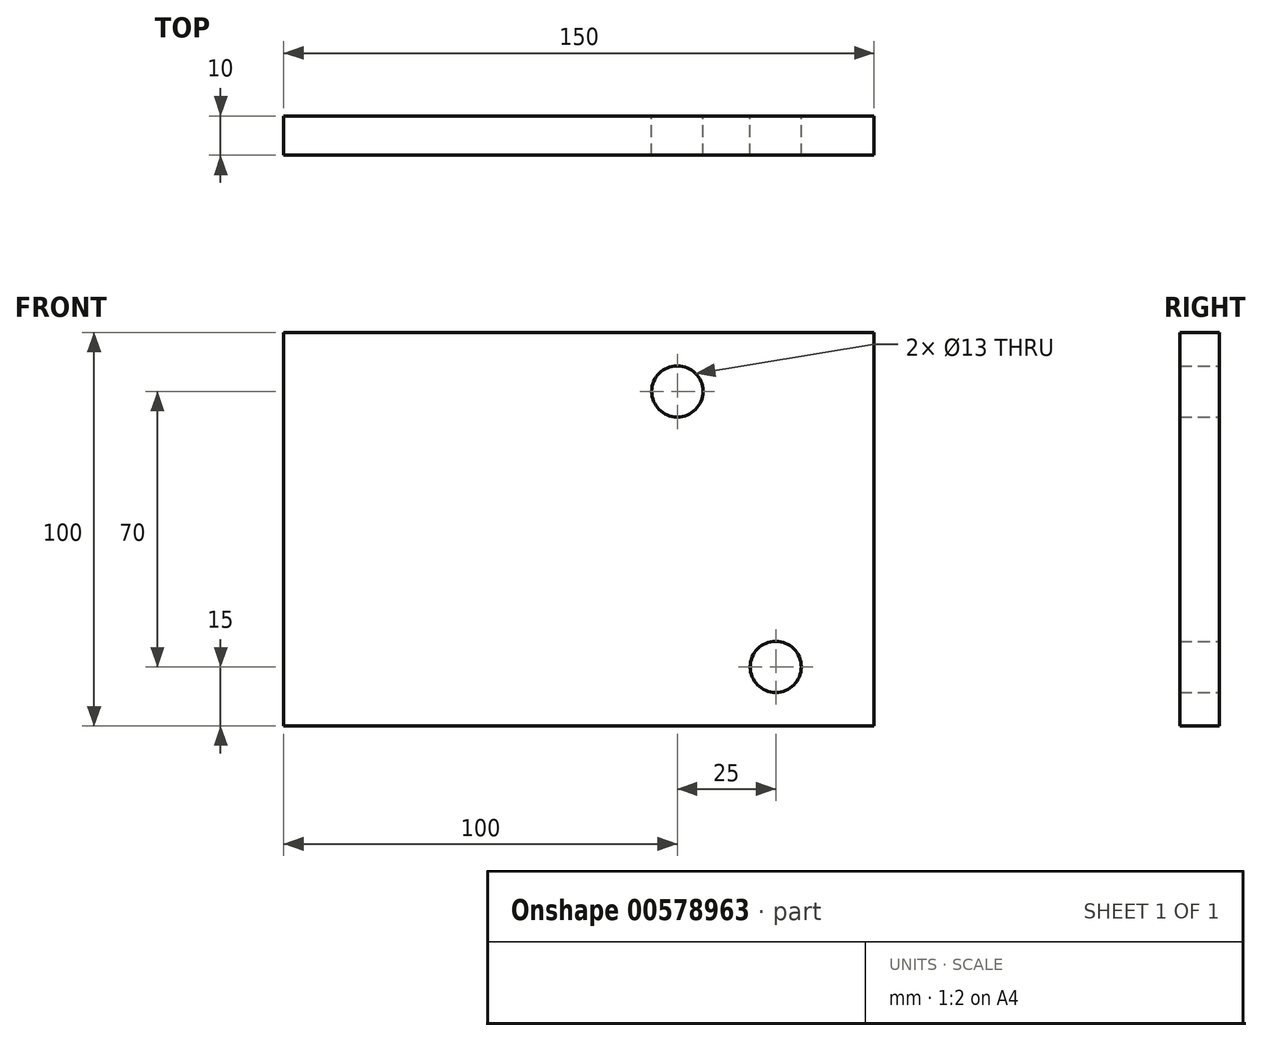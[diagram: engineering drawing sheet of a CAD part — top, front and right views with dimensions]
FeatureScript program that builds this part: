
annotation { "Feature Type Name" : "Feature", "Feature Type Description" : "" }
export const myFeature = defineFeature(function(context is Context, id is Id, definition is map)
    precondition{}
    {
        {
            var Q0;
            Q0=qCreatedBy(makeId("Front.planeOp"),FACE);
            var sketch = newSketch(context, id + "F0", { "sketchPlane" : qUnion([Q0])});
            skLineSegment(sketch, "E0.bottom", {"start": v(75, 50) * mm, "end": v(-75, 50) * mm});
            skLineSegment(sketch, "E0.top", {"start": v(75, -50) * mm, "end": v(-75, -50) * mm});
            skLineSegment(sketch, "E0.left", {"start": v(75, 50) * mm, "end": v(75, -50) * mm});
            skLineSegment(sketch, "E0.right", {"start": v(-75, 50) * mm, "end": v(-75, -50) * mm});
            skPoint(sketch, "E0.middle", {"position": v(0, 0) * mm});
            skCircle(sketch, "E1", {"center": v(50, -35) * mm, "radius": 6.5 * mm});
            skCircle(sketch, "E2", {"center": v(25, 35) * mm, "radius": 6.5 * mm});
            skSolve(sketch);
        }
        {
            var Q0;
            Q0=makeQuery(id+"F0.imprint","IMPRINT",FACE,{"disambiguationData":[TD([[makeQuery(id+"F0.imprint","IMPRINT",EDGE,{"derivedFrom":sQuery(id+"F0.wireOp",EDGE,"E0.bottom")}),1.0]])]});
            extrude(context, id + "F1", {"entities" : qUnion([Q0]), "endBound" : BoundingType.SYMMETRIC, "depth" : 10 * mm, "offsetDistance" : 25 * mm});
        }
    });
